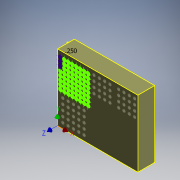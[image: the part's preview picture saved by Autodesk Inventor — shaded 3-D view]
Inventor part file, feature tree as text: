
AUTODESK INVENTOR PART (.ipt)
format: ipt  version: 2018 (Build 220112000, 112)  size: 3,930,624 bytes
history: native  units: mm (DEFAULTED — no unit token found)
features: other x427, loft x121, extrude x18, fillet x5, sketch x4
ambient origin geometry x8: Origin, YZ Plane, XZ Plane, XY Plane, X Axis, Y Axis, Z Axis, Center Point
bodies: Solid1 (feature_tree)
feature tree (575):
  extrude  "Extrusion1"  Depth=127.254mm
  sketch  "Sketch2"  dims[d2=32.004mm d3=0.0mm d4=5.2578mm]
  extrude  "Extrusion2"  Depth=5.2578mm
  extrude  "Extrusion3"  Depth=7.5692mm
  sketch  "Sketch3"  dims[d5=11.6713mm d6=7.5692mm]
  extrude  "Extrusion4"  Depth=7.5692mm
  extrude  "Extrusion5"  Depth=5.2578mm
  extrude  "Extrusion6"  Depth=7.5692mm
  fillet  "Fillet1"  Radius=7.5692mm
  loft  "Loft1"
  loft  "Loft2"
  loft  "Loft3"
  loft  "Loft4"
  loft  "Loft5"
  loft  "Loft6"
  loft  "Loft7"
  loft  "Loft8"
  loft  "Loft9"
  loft  "Loft10"
  loft  "Loft11"
  loft  "Loft12"
  loft  "Loft13"
  loft  "Loft14"
  loft  "Loft15"
  loft  "Loft16"
  loft  "Loft17"
  loft  "Loft18"
  loft  "Loft19"
  loft  "Loft20"
  loft  "Loft21"
  loft  "Loft22"
  loft  "Loft23"
  loft  "Loft24"
  loft  "Loft25"
  loft  "Loft26"
  loft  "Loft27"
  loft  "Loft28"
  loft  "Loft29"
  loft  "Loft30"
  loft  "Loft31"
  loft  "Loft32"
  loft  "Loft33"
  loft  "Loft34"
  loft  "Loft35"
  loft  "Loft36"
  loft  "Loft37"
  loft  "Loft38"
  loft  "Loft39"
  loft  "Loft40"
  loft  "Loft41"
  loft  "Loft42"
  loft  "Loft43"
  loft  "Loft44"
  loft  "Loft45"
  loft  "Loft46"
  loft  "Loft47"
  loft  "Loft48"
  loft  "Loft49"
  loft  "Loft50"
  loft  "Loft51"
  loft  "Loft52"
  loft  "Loft53"
  loft  "Loft54"
  loft  "Loft55"
  loft  "Loft56"
  loft  "Loft57"
  loft  "Loft58"
  loft  "Loft59"
  loft  "Loft60"
  loft  "Loft61"
  loft  "Loft62"
  loft  "Loft63"
  loft  "Loft64"
  sketch  "Sketch4"  dims[d7=5.26mm d8=7.5692mm d9=5.2578mm d10=7.5692mm d11=7.5692mm d12=5.2578mm d13=7.5692mm d14=7.5692mm d15=7.5692mm d16=7.5692mm d17=7.5692mm d18=7.5692mm d19=7.5692mm d20=7.5692mm d21=7.5692mm d22=7.5692mm d23=3.6576mm d24=14.6558mm d25=0.0mm d26=3.6576mm d27=3.6576mm d28=3.6576mm d29=3.6576mm d30=3.6576mm d31=3.6576mm d32=3.6576mm d33=3.6576mm d34=3.6576mm d35=3.6576mm d36=3.6576mm d37=3.6576mm d38=3.6576mm d39=3.6576mm d40=3.6576mm d41=3.6576mm d42=3.6576mm d43=3.6576mm d44=3.6576mm d45=3.6576mm d46=3.6576mm d47=3.6576mm d48=3.6576mm d49=3.6576mm d50=3.6576mm d51=3.6576mm d52=3.6576mm d53=3.6576mm d54=3.6576mm d55=3.6576mm d56=3.6576mm d57=3.6576mm d58=3.6576mm d59=3.6576mm d60=3.6576mm d61=3.6576mm d62=3.6576mm d63=3.6576mm d64=3.6576mm d65=3.6576mm d66=3.6576mm d67=3.6576mm d68=3.6576mm d69=3.6576mm d70=3.6576mm d71=3.6576mm d72=3.6576mm d73=3.6576mm d74=3.6576mm d75=3.6576mm d76=3.6576mm d77=3.6576mm d78=3.6576mm d79=5.8166mm d80=3.6576mm d81=3.6576mm d82=3.6576mm d83=3.6576mm d84=3.6576mm d85=3.6576mm d86=3.6576mm d87=3.6576mm d88=3.6576mm d89=3.6576mm d90=19.812mm d91=0.0mm d92=6.35mm d93=5.8166mm d94=5.8166mm d95=5.8166mm d96=5.8166mm d97=5.8166mm d98=5.8166mm d99=5.8166mm d100=5.8166mm d101=5.8166mm d102=5.8166mm d103=5.8166mm d104=5.8166mm d105=5.8166mm d106=5.8166mm d107=5.8166mm d108=5.8166mm d109=5.8166mm d110=5.8166mm d111=5.8166mm d112=5.8166mm d113=5.8166mm d114=5.8166mm d115=5.8166mm d116=5.8166mm d117=5.8166mm d118=5.8166mm d119=5.8166mm d120=5.8166mm d121=5.8166mm d122=5.8166mm d123=5.8166mm d124=5.8166mm d125=5.8166mm d126=5.8166mm d127=5.8166mm d128=5.8166mm d129=5.8166mm d130=5.8166mm d131=5.8166mm d132=5.8166mm d133=5.8166mm d134=5.8166mm d135=5.8166mm d136=5.8166mm d137=5.8166mm d138=3.6576mm d139=5.8166mm d140=5.8166mm d141=5.8166mm d142=5.8166mm d143=5.8166mm d144=5.8166mm d145=5.8166mm d146=5.8166mm d147=5.8166mm d148=5.8166mm d149=5.8166mm d150=5.8166mm d151=5.8166mm d152=5.8166mm d153=5.8166mm d154=5.8166mm d155=5.8166mm d156=5.8166mm d159=9.398mm d160=0.0mm d161=6.2738mm d162=6.2738mm d163=6.2738mm d164=6.2738mm d165=6.2738mm d166=6.2738mm d167=6.2738mm d168=6.2738mm d169=6.2738mm d170=6.2738mm d171=6.2738mm d172=6.2738mm d173=6.2738mm d174=6.2738mm d175=6.2738mm d176=6.2738mm d177=6.2738mm d178=6.2738mm d179=6.2738mm d180=6.2738mm d181=6.2738mm d182=6.2738mm d183=6.2738mm d184=6.2738mm d185=6.2738mm d186=6.2738mm d187=6.2738mm d188=6.2738mm d189=6.2738mm d190=6.2738mm d191=6.2738mm d192=6.2738mm d193=6.2738mm d194=6.2738mm d195=6.2738mm d196=6.2738mm d197=6.2738mm d198=6.2738mm d199=6.2738mm d200=6.2738mm d201=6.2738mm d202=6.2738mm d203=6.2738mm d204=6.2738mm d205=6.2738mm d206=6.2738mm d207=6.2738mm d208=6.2738mm d209=6.2738mm d210=6.2738mm d211=6.2738mm d212=6.2738mm d213=6.2738mm d214=6.2738mm d215=6.2738mm d216=6.2738mm d217=6.2738mm d218=6.2738mm d219=6.2738mm d220=6.2738mm d221=6.2738mm d222=6.2738mm d223=6.2738mm d224=6.2738mm d225=9.398mm d226=0.0mm d227=6.9596mm d228=6.9596mm d229=6.9596mm d230=6.9596mm d231=6.9596mm d232=6.9596mm d233=6.9596mm d234=6.9596mm d235=6.9596mm d236=6.9596mm d237=6.9596mm d238=6.9596mm d239=6.9596mm d240=6.9596mm d241=6.9596mm d242=6.9596mm d243=6.9596mm d244=6.9596mm d245=6.9596mm d246=6.9596mm d247=6.9596mm d248=6.9596mm d249=6.9596mm d250=6.9596mm d251=6.9596mm d252=6.9596mm d253=6.9596mm d254=6.9596mm d255=6.9596mm d256=6.9596mm d257=6.9596mm d258=6.9596mm d259=6.9596mm d260=6.9596mm d261=6.9596mm d262=6.9596mm d263=6.9596mm d264=6.9596mm d265=6.9596mm d266=6.9596mm d267=6.9596mm d268=6.9596mm d269=6.9596mm d270=6.9596mm d271=6.9596mm d272=6.9596mm d273=6.9596mm d274=6.9596mm d275=6.9596mm d276=6.9596mm d277=6.9596mm d278=6.9596mm d279=6.9596mm d280=6.9596mm d281=6.9596mm d282=6.9596mm d283=6.9596mm d284=6.9596mm d285=6.9596mm d286=6.9596mm d287=6.9596mm d288=6.9596mm d289=6.9596mm d290=6.9596mm d291=4.1148mm d292=0.0mm d293=1.8288mm d294=0.0mm d295=90.0deg d296=0.0mm d297=90.0deg d298=0.0mm d299=90.0deg d300=0.0mm d301=90.0deg d302=0.0mm d303=90.0deg d304=0.0mm d305=90.0deg d306=0.0mm d307=90.0deg d308=0.0mm d309=90.0deg d310=0.0mm d311=90.0deg d312=0.0mm d313=90.0deg d314=0.0mm d315=90.0deg d316=0.0mm d317=90.0deg d318=0.0mm d319=90.0deg d320=0.0mm d321=90.0deg d322=0.0mm d323=90.0deg d324=0.0mm d325=90.0deg d326=0.0mm d327=90.0deg d328=0.0mm d329=90.0deg d330=0.0mm d331=90.0deg d332=0.0mm d333=90.0deg d334=0.0mm d335=90.0deg d336=0.0mm d337=90.0deg d338=0.0mm d339=90.0deg d340=0.0mm d341=90.0deg d342=0.0mm d343=90.0deg d344=0.0mm d345=90.0deg d346=0.0mm d347=90.0deg d348=0.0mm d349=90.0deg d350=0.0mm d351=90.0deg d352=0.0mm d353=90.0deg d354=0.0mm d355=90.0deg d356=0.0mm d357=90.0deg d358=0.0mm d359=90.0deg d360=0.0mm d361=90.0deg d362=0.0mm d363=90.0deg d364=0.0mm d365=90.0deg d366=0.0mm d367=90.0deg d368=0.0mm d369=90.0deg d370=0.0mm d371=90.0deg d372=0.0mm d373=90.0deg d374=0.0mm d375=90.0deg d376=0.0mm d377=90.0deg d378=0.0mm d379=90.0deg d380=0.0mm d381=90.0deg d382=0.0mm d383=90.0deg d384=0.0mm d385=90.0deg d386=0.0mm d387=90.0deg d388=0.0mm d389=90.0deg d390=0.0mm d391=90.0deg d392=0.0mm d393=90.0deg d394=0.0mm d395=90.0deg d396=0.0mm d397=90.0deg d398=0.0mm d399=90.0deg d400=0.0mm d401=90.0deg d402=0.0mm d403=90.0deg d404=0.0mm d405=90.0deg d406=0.0mm d407=90.0deg d408=0.0mm d409=90.0deg d410=0.0mm d411=90.0deg d412=0.0mm d413=90.0deg d414=0.0mm d415=90.0deg d416=0.0mm d417=90.0deg d418=0.0mm d419=90.0deg d420=0.0mm d421=90.0deg d422=0.0mm d423=90.0deg d424=0.0mm d425=90.0deg d426=0.0mm d427=90.0deg d428=0.0mm d429=90.0deg d430=0.0mm d431=90.0deg d432=0.0mm d433=90.0deg d434=0.0mm d435=90.0deg d436=0.0mm d437=90.0deg d438=0.0mm d439=90.0deg d440=0.0mm d441=90.0deg d442=0.0mm d443=90.0deg d444=0.0mm d445=90.0deg d446=0.0mm d447=90.0deg d448=0.0mm d449=90.0deg d450=0.0mm d451=90.0deg d452=0.0mm d453=90.0deg d454=0.0mm d455=90.0deg d456=0.0mm d457=90.0deg d458=0.0mm d459=90.0deg d460=0.0mm d461=90.0deg d462=0.0mm d463=90.0deg d464=0.0mm d465=90.0deg d466=0.0mm d467=90.0deg d468=0.0mm d469=90.0deg d470=0.0mm d471=90.0deg d472=0.0mm d473=90.0deg d474=0.0mm d475=90.0deg d476=0.0mm d477=90.0deg d478=0.0mm d479=90.0deg d480=0.0mm d481=90.0deg d482=0.0mm d483=90.0deg d484=0.0mm d485=90.0deg d486=0.0mm d487=90.0deg d488=0.0mm d489=90.0deg d490=0.0mm d491=90.0deg d492=0.0mm d493=90.0deg d494=0.0mm d495=90.0deg d496=0.0mm d497=90.0deg d498=0.0mm d499=90.0deg d500=0.0mm d501=90.0deg d502=0.0mm d503=90.0deg d504=0.0mm d505=90.0deg d506=0.0mm d507=90.0deg d508=0.0mm d509=90.0deg d510=0.0mm d511=90.0deg d512=0.0mm d513=90.0deg d514=0.0mm d515=90.0deg d516=0.0mm d517=90.0deg d518=0.0mm d519=90.0deg d520=0.0mm d521=90.0deg d522=0.0mm d523=90.0deg d524=0.0mm d525=90.0deg d526=0.0mm d527=90.0deg d528=0.0mm d529=90.0deg d530=0.0mm d531=90.0deg d532=0.0mm d533=90.0deg d534=0.0mm d535=90.0deg d536=0.0mm d537=90.0deg d538=0.0mm d539=90.0deg d540=0.0mm d541=90.0deg d542=0.0mm d543=90.0deg d544=0.0mm d545=90.0deg d546=0.0mm d547=90.0deg d548=0.0mm d549=90.0deg d550=0.0mm d551=90.0deg d552=0.0mm d553=90.0deg d554=0.0mm d555=90.0deg d556=0.0mm d557=90.0deg d558=0.0mm d559=90.0deg d560=0.0mm d561=90.0deg d562=0.0mm d563=90.0deg d564=0.0mm d565=90.0deg d566=0.0mm d567=90.0deg d568=0.0mm d569=90.0deg d570=0.0mm d571=90.0deg d572=0.0mm d573=90.0deg d574=0.0mm d575=90.0deg d576=0.0mm d577=90.0deg d578=0.0mm d579=90.0deg d580=0.0mm d581=90.0deg d582=0.0mm d583=90.0deg d584=0.0mm d585=90.0deg d586=0.0mm d587=90.0deg d588=0.0mm d589=90.0deg d590=0.0mm d591=90.0deg d592=0.0mm d593=90.0deg d594=0.0mm d595=90.0deg d596=0.0mm d597=90.0deg d598=0.0mm d599=90.0deg d600=0.0mm d601=90.0deg d602=0.0mm d603=90.0deg d604=0.0mm d605=90.0deg d606=0.0mm d607=90.0deg d608=0.0mm d609=90.0deg d610=0.0mm d611=90.0deg d612=0.0mm d613=90.0deg d614=0.0mm d615=90.0deg d616=0.0mm d617=90.0deg d618=0.0mm d619=90.0deg d620=0.0mm d621=90.0deg d622=0.0mm d623=90.0deg d624=0.0mm d625=90.0deg d626=0.0mm d627=90.0deg d628=0.0mm d629=90.0deg d630=0.0mm d631=90.0deg d632=0.0mm d633=90.0deg d634=0.0mm d635=90.0deg d636=0.0mm d637=90.0deg d638=0.0mm d639=90.0deg d640=0.0mm d641=90.0deg d642=0.0mm d643=90.0deg d644=0.0mm d645=90.0deg d646=0.0mm d647=90.0deg d648=0.0mm d649=90.0deg d650=0.0mm d651=90.0deg d652=0.0mm d653=90.0deg d654=0.0mm d655=90.0deg d656=0.0mm d657=90.0deg d658=0.0mm d659=90.0deg d660=0.0mm d661=90.0deg d662=0.0mm d663=90.0deg d664=0.0mm d665=90.0deg d666=0.0mm d667=90.0deg d668=0.0mm d669=90.0deg d670=0.0mm d671=90.0deg d672=0.0mm d673=90.0deg d674=0.0mm d675=90.0deg d676=0.0mm d677=90.0deg d678=0.0mm d679=90.0deg d680=0.0mm d681=90.0deg d682=0.0mm d683=90.0deg d684=0.0mm d685=90.0deg d686=0.0mm d687=90.0deg d688=0.0mm d689=90.0deg d690=0.0mm d691=90.0deg d692=0.0mm d693=90.0deg d694=0.0mm d695=90.0deg d696=0.0mm d697=90.0deg d698=0.0mm d699=90.0deg d700=0.0mm d701=90.0deg d702=0.0mm d703=90.0deg d704=0.0mm d705=90.0deg d706=0.0mm d707=90.0deg d708=0.0mm d709=90.0deg d710=0.0mm d711=90.0deg d712=0.0mm d713=90.0deg d714=0.0mm d715=90.0deg d716=0.0mm d717=90.0deg d718=0.0mm d719=90.0deg d720=0.0mm d721=90.0deg d722=0.0mm d723=90.0deg d724=0.0mm d725=90.0deg d726=0.0mm d727=90.0deg d728=0.0mm d729=90.0deg d730=0.0mm d731=90.0deg d732=0.0mm d733=90.0deg d734=0.0mm d735=90.0deg d736=0.0mm d737=90.0deg d738=0.0mm d739=90.0deg d740=0.0mm d741=90.0deg d742=0.0mm d743=90.0deg d744=0.0mm d745=90.0deg d746=0.0mm d747=90.0deg d748=0.0mm d749=90.0deg d750=0.0mm d751=90.0deg d752=0.0mm d753=90.0deg d754=0.0mm d755=90.0deg d756=0.0mm d757=90.0deg d758=0.0mm d759=90.0deg d760=0.0mm d761=90.0deg d762=0.0mm d763=90.0deg d764=0.0mm d765=90.0deg d766=0.0mm d767=90.0deg d768=0.0mm d769=90.0deg d770=0.0mm d771=90.0deg d772=0.0mm d773=90.0deg d774=0.0mm d775=90.0deg d776=0.0mm d777=90.0deg d778=0.0mm d779=90.0deg d780=0.0mm d781=90.0deg d782=0.0mm d783=90.0deg d784=0.0mm d785=90.0deg d786=0.0mm d787=90.0deg d788=0.0mm d789=90.0deg d790=0.0mm d791=90.0deg d792=0.0mm d793=90.0deg d794=0.0mm d795=90.0deg d796=0.0mm d797=90.0deg d798=0.0mm d799=90.0deg d800=0.0mm d801=90.0deg d802=0.0mm d803=90.0deg d804=0.0mm d805=90.0deg d806=10.16mm d807=10.16mm d808=10.16mm d809=10.16mm d810=10.16mm d811=10.16mm d812=10.16mm d813=3.3147mm d814=3.3147mm d815=3.3147mm d816=3.3147mm d817=3.3147mm d818=3.3147mm d819=3.3147mm d820=3.3147mm d821=3.3147mm d822=3.3147mm d823=3.3147mm d824=3.3147mm d825=3.3147mm d826=3.3147mm d827=3.3147mm d828=3.3147mm d829=5.6642mm d830=5.6642mm d831=5.6642mm d832=5.6642mm d833=5.6642mm d834=5.6642mm d835=5.6642mm d836=5.6642mm d837=5.6642mm d838=5.6642mm d839=5.6642mm d840=5.6642mm d841=5.6642mm d842=5.6642mm d843=5.6642mm d844=5.6642mm d845=6.2865mm d846=19.6215mm d847=0.0mm d848=9.2837mm d849=0.0mm d850=0.8128mm d851=0.00254mm d852=0.0mm d853=0.0mm d854=90.0deg d855=0.0mm d856=90.0deg d857=0.0mm d858=90.0deg d859=6.2865mm d860=6.2865mm d861=6.2865mm d862=6.2865mm d863=6.2865mm d864=6.2865mm d865=6.2865mm d866=6.2865mm d867=6.2865mm d868=6.2865mm d869=6.2865mm d870=6.2865mm d871=6.2865mm d872=6.2865mm d873=6.2865mm d874=19.6215mm d875=0.0mm d876=9.2837mm d877=0.0mm d878=0.00254mm d879=0.0mm d880=0.8128mm d881=0.0mm d882=90.0deg d883=0.0mm d884=90.0deg d885=0.0mm d886=90.0deg d887=0.0mm d888=90.0deg d889=0.0mm d890=90.0deg d891=0.0mm d892=90.0deg d893=0.0mm d894=90.0deg d895=0.0mm d896=90.0deg d897=0.0mm d898=90.0deg d899=0.0mm d900=90.0deg d901=0.0mm d902=90.0deg d903=0.0mm d904=90.0deg d905=0.0mm d906=90.0deg d907=0.0mm d908=90.0deg d909=0.0mm d910=90.0deg d911=0.0mm d912=90.0deg d913=0.0mm d914=90.0deg d915=0.0mm d916=90.0deg d917=0.0mm d918=90.0deg d919=0.0mm d920=90.0deg d921=0.0mm d922=90.0deg d923=0.0mm d924=90.0deg d925=0.0mm d926=90.0deg d927=0.0mm d928=90.0deg d929=0.0mm d930=90.0deg d931=0.0mm d932=90.0deg d933=0.0mm d934=90.0deg d935=0.0mm d936=90.0deg d937=0.0mm d938=90.0deg d939=0.0mm d940=90.0deg d941=0.0mm d942=90.0deg d943=0.0mm d944=90.0deg d945=0.0mm d946=90.0deg d947=0.0mm d948=90.0deg d949=0.0mm d950=90.0deg d951=0.0mm d952=90.0deg d953=0.0mm d954=90.0deg d955=0.0mm d956=90.0deg d957=0.0mm d958=90.0deg d959=0.0mm d960=90.0deg d961=0.0mm d962=90.0deg d963=0.0mm d964=90.0deg d965=0.0mm d966=90.0deg d967=0.0mm d968=90.0deg d969=0.0mm d970=90.0deg d971=16.51mm d972=10.16mm d973=10.16mm d974=10.16mm d975=6.2865mm d976=6.2865mm d977=6.2865mm d978=6.2865mm d979=6.2865mm d980=6.2865mm d981=6.2865mm d982=6.2865mm d983=6.2865mm d984=6.2865mm d985=6.2865mm d986=6.2865mm d987=6.2865mm d988=6.2865mm d989=6.2865mm d990=6.2865mm d991=5.6642mm d992=5.6642mm d993=5.6642mm d994=5.6642mm d995=5.6642mm d996=5.6642mm d997=5.6642mm d998=5.6642mm d999=5.6642mm d1000=5.6642mm d1001=5.6642mm d1002=5.6642mm d1003=5.6642mm d1004=5.6642mm d1005=5.6642mm d1006=5.6642mm d1007=3.3147mm d1008=3.3147mm d1009=3.3147mm d1010=3.3147mm d1011=3.3147mm d1012=3.3147mm d1013=3.3147mm d1014=3.3147mm d1015=3.3147mm d1016=3.3147mm d1017=3.3147mm d1018=3.3147mm d1019=3.3147mm d1020=3.3147mm d1021=3.3147mm d1022=3.3147mm d1023=20.1803mm d1024=0.0mm d1025=9.2837mm d1026=0.0mm d1027=0.00254mm d1028=0.0mm d1029=0.8128mm d1030=0.0mm d1031=90.0deg d1032=0.0mm d1033=90.0deg d1034=0.0mm d1035=90.0deg d1036=0.0mm d1037=90.0deg d1038=0.0mm d1039=90.0deg d1040=0.0mm d1041=90.0deg d1042=0.0mm d1043=90.0deg d1044=0.0mm d1045=90.0deg d1046=0.0mm d1047=90.0deg d1048=0.0mm d1049=90.0deg d1050=0.0mm d1051=90.0deg d1052=0.0mm d1053=90.0deg d1054=0.0mm d1055=90.0deg d1056=0.0mm d1057=90.0deg d1058=0.0mm d1059=90.0deg d1060=0.0mm d1061=90.0deg d1062=0.0mm d1063=90.0deg d1064=0.0mm d1065=90.0deg d1066=0.0mm d1067=90.0deg d1068=0.0mm d1069=90.0deg d1070=0.0mm d1071=90.0deg d1072=0.0mm d1073=90.0deg d1074=0.0mm d1075=90.0deg d1076=0.0mm d1077=90.0deg d1078=0.0mm d1079=90.0deg d1080=0.0mm d1081=90.0deg d1082=0.0mm d1083=90.0deg d1084=0.0mm d1085=90.0deg d1086=0.0mm d1087=90.0deg d1088=0.0mm d1089=90.0deg d1090=0.0mm d1091=90.0deg d1092=0.0mm d1093=90.0deg d1094=0.0mm d1095=90.0deg d1096=0.0mm d1097=90.0deg d1098=0.0mm d1099=90.0deg d1100=0.0mm d1101=90.0deg d1102=0.0mm d1103=90.0deg d1104=0.0mm d1105=90.0deg d1106=0.0mm d1107=90.0deg d1108=0.0mm d1109=90.0deg d1110=0.0mm d1111=90.0deg d1112=0.0mm d1113=90.0deg d1114=0.0mm d1115=90.0deg d1116=0.0mm d1117=90.0deg d1118=0.0mm d1119=90.0deg d1120=0.0mm d1121=90.0deg d1122=0.0mm d1123=90.0deg d1124=0.0mm d1125=90.0deg d1126=10.16mm d1127=10.16mm d1128=10.16mm d1129=10.16mm d1130=10.16mm d1131=10.16mm d1132=10.16mm d1133=10.16mm d1134=10.16mm d1135=10.16mm d1136=10.16mm d1137=10.16mm d1138=6.2865mm d1139=6.2865mm d1140=6.2865mm d1141=6.2865mm d1142=6.2865mm d1143=6.2865mm d1144=6.2865mm d1145=6.2865mm d1146=6.2865mm d1147=6.2865mm d1148=6.2865mm d1149=6.2865mm d1150=6.2865mm d1151=6.2865mm d1152=6.2865mm d1153=6.2865mm d1154=10.16mm d1155=10.16mm d1156=6.2865mm d1157=6.2865mm d1158=6.2865mm d1159=6.2865mm d1160=6.2865mm d1161=6.2865mm d1162=6.2865mm d1163=6.2865mm d1164=6.2865mm d1165=5.6642mm d1166=5.6642mm d1167=5.6642mm d1168=5.6642mm d1169=5.6642mm d1170=5.6642mm d1171=5.6642mm d1172=5.6642mm d1173=5.6642mm d1174=5.6642mm d1175=5.6642mm d1176=5.6642mm d1177=5.6642mm d1178=5.6642mm d1179=5.6642mm d1180=5.6642mm d1181=5.6642mm d1182=5.6642mm d1183=5.6642mm d1184=5.6642mm d1185=5.6642mm d1186=5.6642mm d1187=5.6642mm d1188=5.6642mm d1189=5.6642mm d1190=3.3147mm d1191=3.3147mm d1192=3.3147mm d1193=3.3147mm d1194=3.3147mm d1195=3.3147mm d1196=3.3147mm d1197=3.3147mm d1198=3.3147mm d1199=3.3147mm d1200=3.3147mm d1201=3.3147mm d1202=3.3147mm d1203=3.3147mm d1204=3.3147mm d1205=3.3147mm d1206=3.3147mm d1207=3.3147mm d1208=3.3147mm d1209=3.3147mm d1210=3.3147mm d1211=3.3147mm d1212=3.3147mm d1213=3.3147mm d1214=3.3147mm d1215=20.1803mm d1216=0.0mm d1217=9.2837mm d1218=0.0mm d1219=0.00254mm d1220=0.0mm d1221=0.8128mm d1222=0.0mm d1223=90.0deg d1224=0.0mm d1225=90.0deg d1226=0.0mm d1227=90.0deg d1228=0.0mm d1229=90.0deg d1230=0.0mm d1231=90.0deg d1232=0.0mm d1233=90.0deg d1234=0.0mm d1235=90.0deg d1236=0.0mm d1237=90.0deg d1238=0.0mm d1239=90.0deg d1240=0.0mm d1241=90.0deg d1242=0.0mm d1243=90.0deg d1244=0.0mm d1245=90.0deg d1246=0.0mm d1247=90.0deg d1248=0.0mm d1249=90.0deg d1250=0.0mm d1251=90.0deg d1252=0.0mm d1253=90.0deg d1254=0.0mm d1255=90.0deg d1256=0.0mm d1257=90.0deg d1258=0.0mm d1259=90.0deg d1260=0.0mm d1261=90.0deg d1262=0.0mm d1263=90.0deg d1264=0.0mm d1265=90.0deg d1266=0.0mm d1267=90.0deg d1268=0.0mm d1269=90.0deg d1270=0.0mm d1271=90.0deg d1272=0.0mm d1273=90.0deg d1274=0.0mm d1275=90.0deg d1276=0.0mm d1277=90.0deg d1278=0.0mm d1279=90.0deg d1280=0.0mm d1281=90.0deg d1282=0.0mm d1283=90.0deg d1284=0.0mm d1285=90.0deg d1286=0.0mm d1287=90.0deg d1288=0.0mm d1289=90.0deg d1290=0.0mm d1291=90.0deg d1292=0.0mm d1293=90.0deg d1294=0.0mm d1295=90.0deg d1296=0.0mm d1297=90.0deg d1298=0.0mm d1299=90.0deg d1300=0.0mm d1301=90.0deg d1302=0.0mm d1303=90.0deg d1304=0.0mm d1305=90.0deg d1306=0.0mm d1307=90.0deg d1308=0.0mm d1309=90.0deg d1310=0.0mm d1311=90.0deg d1312=0.0mm d1313=90.0deg d1314=0.0mm d1315=90.0deg d1316=0.0mm d1317=90.0deg d1318=0.0mm d1319=90.0deg d1320=0.0mm d1321=90.0deg d1322=0.0mm d1323=90.0deg d1324=0.0mm d1325=90.0deg d1326=0.0mm d1327=90.0deg d1328=0.0mm d1329=90.0deg d1330=0.0mm d1331=90.0deg d1332=0.0mm d1333=90.0deg d1334=0.0mm d1335=90.0deg d1336=0.0mm d1337=90.0deg d1338=0.0mm d1339=90.0deg d1340=0.0mm d1341=90.0deg d1342=0.0mm d1343=90.0deg d1344=0.0mm d1345=90.0deg d1346=0.0mm d1347=90.0deg d1348=0.0mm d1349=90.0deg d1350=0.0mm d1351=90.0deg d1352=0.0mm d1353=90.0deg d1354=0.0mm d1355=90.0deg d1356=0.0mm d1357=90.0deg d1358=0.0mm d1359=90.0deg d1360=0.0mm d1361=90.0deg d1362=0.0mm d1363=90.0deg d1364=0.0mm d1365=90.0deg d1366=0.0mm d1367=90.0deg d1368=0.0mm d1369=90.0deg d1370=0.0mm d1371=90.0deg]
  extrude  "Extrusion7"  Depth=3.6576mm
  extrude  "Extrusion8"  Depth=3.6576mm
  fillet  "Fillet2"  Radius=5.8166mm
  extrude  "Extrusion9"  Depth=3.6576mm
  loft  "Loft65"
  extrude  "Extrusion10"  Depth=3.6576mm
  extrude  "Extrusion11"  Depth=3.6576mm
  extrude  "Extrusion12"  Depth=3.6576mm
  fillet  "Fillet3"  Radius=3.6576mm
  loft  "Loft66"
  loft  "Loft67"
  loft  "Loft68"
  loft  "Loft69"
  loft  "Loft70"
  loft  "Loft71"
  loft  "Loft72"
  loft  "Loft73"
  loft  "Loft74"
  loft  "Loft75"
  loft  "Loft76"
  loft  "Loft77"
  loft  "Loft78"
  loft  "Loft79"
  loft  "Loft80"
  extrude  "Extrusion13"  Depth=5.8166mm
  extrude  "Extrusion14"  Depth=5.8166mm
  extrude  "Extrusion15"  Depth=5.8166mm
  fillet  "Fillet4"  Radius=5.8166mm
  loft  "Loft81"
  loft  "Loft82"
  loft  "Loft83"
  loft  "Loft84"
  loft  "Loft85"
  loft  "Loft86"
  loft  "Loft87"
  loft  "Loft88"
  loft  "Loft89"
  loft  "Loft90"
  loft  "Loft91"
  loft  "Loft92"
  loft  "Loft93"
  loft  "Loft94"
  loft  "Loft95"
  loft  "Loft96"
  extrude  "Extrusion16"  Depth=5.8166mm
  extrude  "Extrusion17"  Depth=5.8166mm
  extrude  "Extrusion18"  Depth=5.8166mm
  fillet  "Fillet5"  Radius=5.8166mm
  loft  "Loft97"
  loft  "Loft98"
  loft  "Loft99"
  loft  "Loft100"
  loft  "Loft101"
  loft  "Loft102"
  loft  "Loft103"
  loft  "Loft104"
  loft  "Loft105"
  loft  "Loft106"
  loft  "Loft107"
  loft  "Loft108"
  loft  "Loft109"
  loft  "Loft110"
  loft  "Loft111"
  loft  "Loft112"
  loft  "Loft113"
  loft  "Loft114"
  loft  "Loft115"
  loft  "Loft116"
  loft  "Loft117"
  loft  "Loft118"
  loft  "Loft119"
  loft  "Loft120"
  loft  "Loft121"
  sketch  "Sketch1"  dims[d0=153.162mm d1=127.254mm]
  other  "Edges1"
  other  "Edges2"
  other  "Edges3"
  other  "Edges4"
  other  "Edges5"
  other  "Edges6"
  other  "Edges7"
  other  "Edges8"
  other  "Edges9"
  other  "Edges10"
  other  "Edges11"
  other  "Edges12"
  other  "Edges13"
  other  "Edges14"
  other  "Edges15"
  other  "Edges16"
  other  "Edges17"
  other  "Edges18"
  other  "Edges19"
  other  "Edges20"
  other  "Edges21"
  other  "Edges22"
  other  "Edges23"
  other  "Edges24"
  other  "Edges25"
  other  "Edges26"
  other  "Edges27"
  other  "Edges28"
  other  "Edges29"
  other  "Edges30"
  other  "Edges31"
  other  "Edges32"
  other  "Edges33"
  other  "Edges34"
  other  "Edges35"
  other  "Edges36"
  other  "Edges37"
  other  "Edges38"
  other  "Edges39"
  other  "Edges40"
  other  "Edges41"
  other  "Edges42"
  other  "Edges43"
  other  "Edges44"
  other  "Edges45"
  other  "Edges46"
  other  "Edges47"
  other  "Edges48"
  other  "Edges49"
  other  "Edges50"
  other  "Edges51"
  other  "Edges52"
  other  "Edges53"
  other  "Edges54"
  other  "Edges55"
  other  "Edges56"
  other  "Edges57"
  other  "Edges58"
  other  "Edges59"
  other  "Edges60"
  other  "Edges61"
  other  "Edges62"
  other  "Edges63"
  other  "Edges64"
  other  "Edges65"
  other  "Edges66"
  other  "Edges67"
  other  "Edges68"
  other  "Edges69"
  other  "Edges70"
  other  "Edges71"
  other  "Edges72"
  other  "Edges73"
  other  "Edges74"
  other  "Edges75"
  other  "Edges76"
  other  "Edges77"
  other  "Edges78"
  other  "Edges79"
  other  "Edges80"
  other  "Edges81"
  other  "Edges82"
  other  "Edges83"
  other  "Edges84"
  other  "Edges85"
  other  "Edges86"
  other  "Edges87"
  other  "Edges88"
  other  "Edges89"
  other  "Edges90"
  other  "Edges91"
  other  "Edges92"
  other  "Edges93"
  other  "Edges94"
  other  "Edges95"
  other  "Edges96"
  other  "Edges97"
  other  "Edges98"
  other  "Edges99"
  other  "Edges100"
  other  "Edges101"
  other  "Edges102"
  other  "Edges103"
  other  "Edges104"
  other  "Edges105"
  other  "Edges106"
  other  "Edges107"
  other  "Edges108"
  other  "Edges109"
  other  "Edges110"
  other  "Edges111"
  other  "Edges112"
  other  "Edges113"
  other  "Edges114"
  other  "Edges115"
  other  "Edges116"
  other  "Edges117"
  other  "Edges118"
  other  "Edges119"
  other  "Edges120"
  other  "Edges121"
  other  "Edges122"
  other  "Edges123"
  other  "Edges124"
  other  "Edges125"
  other  "Edges126"
  other  "Edges127"
  other  "Edges128"
  other  "Edges129"
  other  "Edges130"
  other  "Edges131"
  other  "Edges132"
  other  "Edges133"
  other  "Edges134"
  other  "Edges135"
  other  "Edges136"
  other  "Edges137"
  other  "Edges138"
  other  "Edges139"
  other  "Edges140"
  other  "Edges141"
  other  "Edges142"
  other  "Edges143"
  other  "Edges144"
  other  "Edges145"
  other  "Edges146"
  other  "Edges147"
  other  "Edges148"
  other  "Edges149"
  other  "Edges150"
  other  "Edges151"
  other  "Edges152"
  other  "Edges153"
  other  "Edges154"
  other  "Edges155"
  other  "Edges156"
  other  "Edges157"
  other  "Edges158"
  other  "Edges159"
  other  "Edges160"
  other  "Edges161"
  other  "Edges162"
  other  "Edges163"
  other  "Edges164"
  other  "Edges165"
  other  "Edges166"
  other  "Edges167"
  other  "Edges168"
  other  "Edges169"
  other  "Edges170"
  other  "Edges171"
  other  "Edges172"
  other  "Edges173"
  other  "Edges174"
  other  "Edges175"
  other  "Edges176"
  other  "Edges177"
  other  "Edges178"
  other  "Edges179"
  other  "Edges180"
  other  "Edges181"
  other  "Edges182"
  other  "Edges183"
  other  "Edges184"
  other  "Edges185"
  other  "Edges186"
  other  "Edges187"
  other  "Edges188"
  other  "Edges189"
  other  "Edges190"
  other  "Edges191"
  other  "Edges192"
  other  "Edges193"
  other  "Edges194"
  other  "Edges195"
  other  "Edges196"
  other  "Edges197"
  other  "Edges198"
  other  "Edges199"
  other  "Edges200"
  other  "Edges201"
  other  "Edges202"
  other  "Edges203"
  other  "Edges204"
  other  "Edges205"
  other  "Edges206"
  other  "Edges207"
  other  "Edges208"
  other  "Edges209"
  other  "Edges210"
  other  "Edges211"
  other  "Edges212"
  other  "Edges213"
  other  "Edges214"
  other  "Edges215"
  other  "Edges216"
  other  "Edges217"
  other  "Edges218"
  other  "Edges219"
  other  "Edges220"
  other  "Edges221"
  other  "Edges222"
  other  "Edges223"
  other  "Edges224"
  other  "Edges225"
  other  "Edges226"
  other  "Edges227"
  other  "Edges228"
  other  "Edges229"
  other  "Edges230"
  other  "Edges231"
  other  "Edges232"
  other  "Edges233"
  other  "Edges234"
  other  "Edges235"
  other  "Edges236"
  other  "Edges237"
  other  "Edges238"
  other  "Edges239"
  other  "Edges240"
  other  "Edges241"
  other  "Edges242"
  other  "Edges243"
  other  "Edges244"
  other  "Edges245"
  other  "Edges246"
  other  "Edges247"
  other  "Edges248"
  other  "Edges249"
  other  "Edges250"
  other  "Edges251"
  other  "Edges252"
  other  "Edges253"
  other  "Edges254"
  other  "Edges255"
  other  "Edges256"
  other  "Edges257"
  other  "Edges258"
  other  "Edges259"
  other  "Edges260"
  other  "Edges261"
  other  "Edges262"
  other  "Edges263"
  other  "Edges264"
  other  "Edges265"
  other  "Edges266"
  other  "Edges267"
  other  "Edges268"
  other  "Edges269"
  other  "Edges270"
  other  "Edges271"
  other  "Edges272"
  other  "Edges273"
  other  "Edges274"
  other  "Edges275"
  other  "Edges276"
  other  "Edges277"
  other  "Edges278"
  other  "Edges279"
  other  "Edges280"
  other  "Edges281"
  other  "Edges282"
  other  "Edges283"
  other  "Edges284"
  other  "Edges285"
  other  "Edges286"
  other  "Edges287"
  other  "Edges288"
  other  "Edges289"
  other  "Edges290"
  other  "Edges291"
  other  "Edges292"
  other  "Edges293"
  other  "Edges294"
  other  "Edges295"
  other  "Edges296"
  other  "Edges297"
  other  "Edges298"
  other  "Edges299"
  other  "Edges300"
  other  "Edges301"
  other  "Edges302"
  other  "Edges303"
  other  "Edges304"
  other  "Edges305"
  other  "Edges306"
  other  "Edges307"
  other  "Edges308"
  other  "Edges309"
  other  "Edges310"
  other  "Edges311"
  other  "Edges312"
  other  "Edges313"
  other  "Edges314"
  other  "Edges315"
  other  "Edges316"
  other  "Edges317"
  other  "Edges318"
  other  "Edges319"
  other  "Edges320"
  other  "Edges321"
  other  "Edges322"
  other  "Edges323"
  other  "Edges324"
  other  "Edges325"
  other  "Edges326"
  other  "Edges327"
  other  "Edges328"
  other  "Edges329"
  other  "Edges330"
  other  "Edges331"
  other  "Edges332"
  other  "Edges333"
  other  "Edges334"
  other  "Edges335"
  other  "Edges336"
  other  "Edges337"
  other  "Edges338"
  other  "Edges339"
  other  "Edges340"
  other  "Edges341"
  other  "Edges342"
  other  "Edges343"
  other  "Edges344"
  other  "Edges345"
  other  "Edges346"
  other  "Edges347"
  other  "Edges348"
  other  "Edges349"
  other  "Edges350"
  other  "Edges351"
  other  "Edges352"
  other  "Edges353"
  other  "Edges354"
  other  "Edges355"
  other  "Edges356"
  other  "Edges357"
  other  "Edges358"
  other  "Edges359"
  other  "Edges360"
  other  "Edges361"
  other  "Edges362"
  other  "Edges363"
  other  "Edges364"
  other  "Edges365"
  other  "Edges366"
  other  "Edges367"
  other  "Edges368"
  other  "Edges369"
  other  "Edges370"
  other  "Edges371"
  other  "Edges372"
  other  "Edges373"
  other  "Edges374"
  other  "Edges375"
  other  "Edges376"
  other  "Edges377"
  other  "Edges378"
  other  "Edges379"
  other  "Edges380"
  other  "Edges381"
  other  "Edges382"
  other  "Edges383"
  other  "Edges384"
  other  "Edges385"
  other  "Edges386"
  other  "Edges387"
  other  "Edges388"
  other  "Edges389"
  other  "Edges390"
  other  "Edges391"
  other  "Edges392"
  other  "Edges393"
  other  "Edges394"
  other  "Edges395"
  other  "Edges396"
  other  "Edges397"
  other  "Edges398"
  other  "Edges399"
  other  "Edges400"
  other  "Edges401"
  other  "Edges402"
  other  "Edges403"
  other  "Edges404"
  other  "Edges405"
  other  "Edges406"
  other  "Edges407"
  other  "Edges408"
  other  "Edges409"
  other  "Edges410"
  other  "Edges411"
  other  "Edges412"
  other  "Edges413"
  other  "Edges414"
  other  "Edges415"
  other  "Edges416"
  other  "Edges417"
  other  "Edges418"
  other  "Edges419"
  other  "Edges420"
  other  "Edges421"
  other  "Edges422"
  other  "Edges423"
  other  "Edges424"
  other  "Edges425"
  other  "Edges426"
  other  "Edges427"
